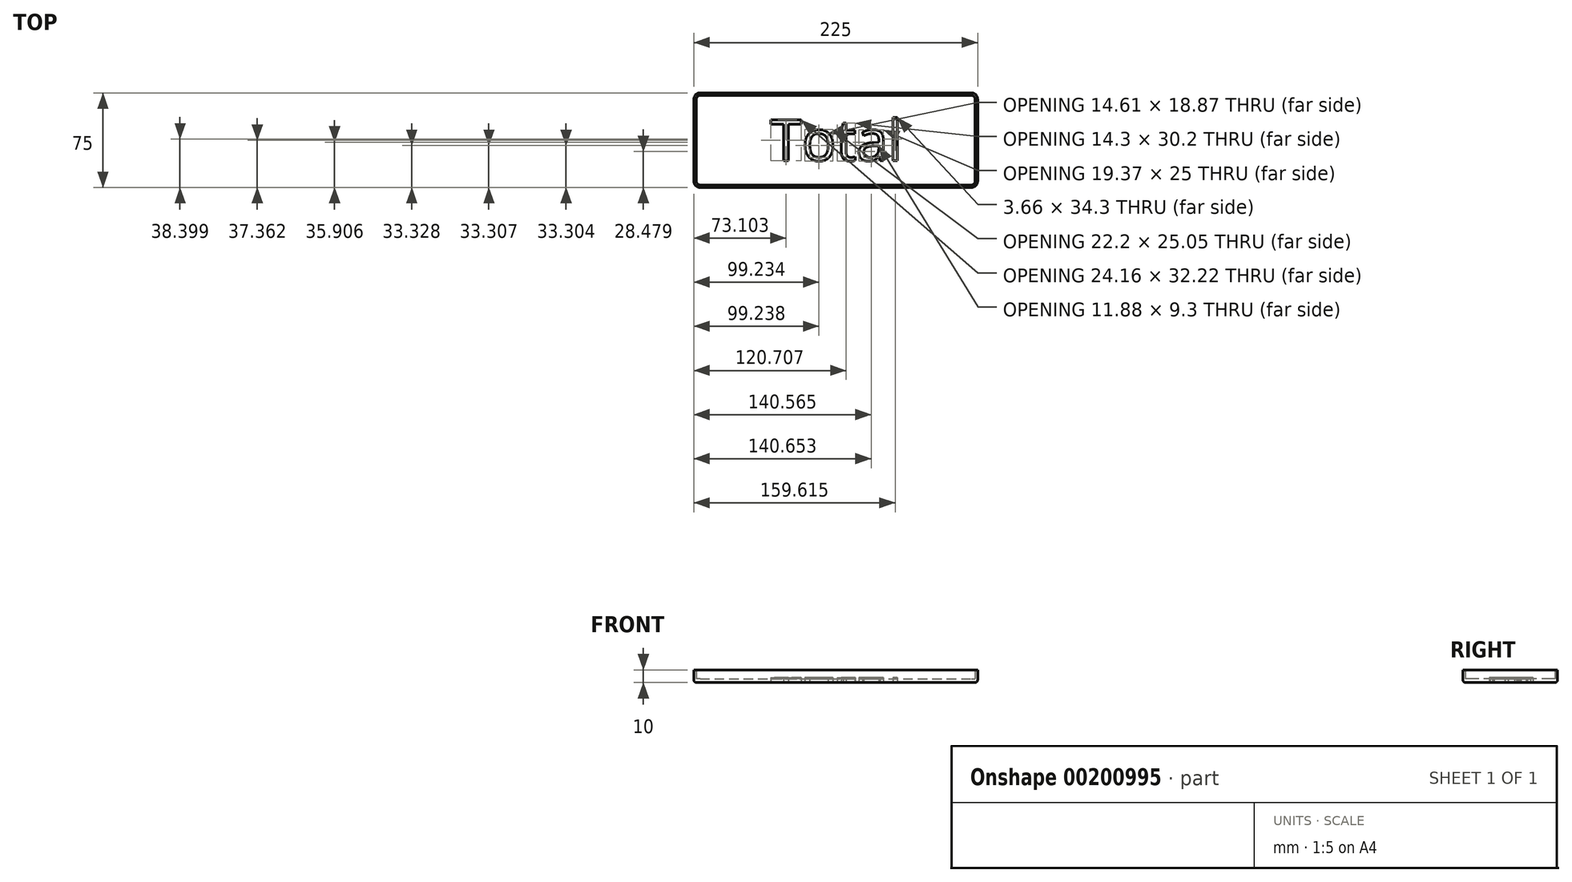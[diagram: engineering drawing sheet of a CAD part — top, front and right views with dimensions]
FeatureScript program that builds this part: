
annotation { "Feature Type Name" : "Feature", "Feature Type Description" : "" }
export const myFeature = defineFeature(function(context is Context, id is Id, definition is map)
    precondition{}
    {
        {
            var Q0;
            Q0=qCreatedBy(makeId("Top.planeOp"),FACE);
            var sketch = newSketch(context, id + "F0", { "sketchPlane" : qUnion([Q0])});
            skLineSegment(sketch, "E0.bottom", {"start": v(-41.61, 75) * mm, "end": v(173.39, 75) * mm});
            skLineSegment(sketch, "E0.top", {"start": v(-41.61, 0) * mm, "end": v(173.39, 0) * mm});
            skLineSegment(sketch, "E0.left", {"start": v(-46.61, 70) * mm, "end": v(-46.61, 5) * mm});
            skLineSegment(sketch, "E0.right", {"start": v(178.39, 70) * mm, "end": v(178.39, 5) * mm});
            skLineSegment(sketch, "E1.0", {"start": v(-41.61, 2) * mm, "end": v(173.39, 2) * mm});
            skLineSegment(sketch, "E1.1", {"start": v(-44.61, 70) * mm, "end": v(-44.61, 5) * mm});
            skLineSegment(sketch, "E1.2", {"start": v(-41.61, 73) * mm, "end": v(173.39, 73) * mm});
            skLineSegment(sketch, "E1.3", {"start": v(176.39, 70) * mm, "end": v(176.39, 5) * mm});
            skLineSegment(sketch, "E2", {"start": v(65.89, 73) * mm, "end": v(65.89, 2) * mm, "construction": true});
            skText(sketch, "E3", { "text": "Total", "fontName": "OpenSans-Regular.ttf"});
            skLineSegment(sketch, "E4", {"start": v(117.76, 37.5) * mm, "end": v(14.02, 37.5) * mm, "construction": true});
            skLineSegment(sketch, "E5", {"start": v(65.89, 37.5) * mm, "end": v(176.39, 37.5) * mm, "construction": true});
            skPoint(sketch, "E6.visualSharp", {"position": v(176.39, 73) * mm});
            skArc(sketch, "E6.filletArc", {"start": v(176.39, 70) * mm, "mid": v(175.5, 72.12) * mm, "end": v(173.39, 73) * mm});
            skPoint(sketch, "E7.visualSharp", {"position": v(-44.61, 73) * mm});
            skArc(sketch, "E7.filletArc", {"start": v(-41.61, 73) * mm, "mid": v(-43.73, 72.12) * mm, "end": v(-44.61, 70) * mm});
            skPoint(sketch, "E8.visualSharp", {"position": v(-44.61, 2) * mm});
            skArc(sketch, "E8.filletArc", {"start": v(-44.61, 5) * mm, "mid": v(-43.73, 2.88) * mm, "end": v(-41.61, 2) * mm});
            skPoint(sketch, "E9.visualSharp", {"position": v(176.39, 2) * mm});
            skArc(sketch, "E9.filletArc", {"start": v(173.39, 2) * mm, "mid": v(175.5, 2.88) * mm, "end": v(176.39, 5) * mm});
            skPoint(sketch, "E10.visualSharp", {"position": v(178.39, 0) * mm});
            skArc(sketch, "E10.filletArc", {"start": v(173.39, 0) * mm, "mid": v(176.92, 1.46) * mm, "end": v(178.39, 5) * mm});
            skPoint(sketch, "E11.visualSharp", {"position": v(178.39, 75) * mm});
            skArc(sketch, "E11.filletArc", {"start": v(178.39, 70) * mm, "mid": v(176.92, 73.54) * mm, "end": v(173.39, 75) * mm});
            skPoint(sketch, "E12.visualSharp", {"position": v(-46.61, 75) * mm});
            skArc(sketch, "E12.filletArc", {"start": v(-41.61, 75) * mm, "mid": v(-45.15, 73.54) * mm, "end": v(-46.61, 70) * mm});
            skPoint(sketch, "E13.visualSharp", {"position": v(-46.61, 0) * mm});
            skArc(sketch, "E13.filletArc", {"start": v(-46.61, 5) * mm, "mid": v(-45.15, 1.46) * mm, "end": v(-41.61, 0) * mm});
            const initialGuessF0  = {"E3": [0.01402, 0.02125, 1, 0, 0.0325]};
            skSetInitialGuess(sketch, initialGuessF0);
            skSolve(sketch);
        }
        {
            var Q0;
            Q0=makeQuery(id+"F0.imprint","IMPRINT",FACE,{"disambiguationData":[TD([[makeQuery(id+"F0.imprint","IMPRINT",EDGE,{"derivedFrom":sQuery(id+"F0.wireOp",EDGE,"E1.0")}),1.0]])]});
            var Q1;
            Q1=makeQuery(id+"F0.imprint","IMPRINT",FACE,{"disambiguationData":[TD([[makeQuery(id+"F0.imprint","IMPRINT",EDGE,{"derivedFrom":sQuery(id+"F0.wireOp",EDGE,"E3.sketch_text.stroke-63")}),1.0]])]});
            var Q2;
            Q2=makeQuery(id+"F0.imprint","IMPRINT",FACE,{"disambiguationData":[TD([[makeQuery(id+"F0.imprint","IMPRINT",EDGE,{"derivedFrom":sQuery(id+"F0.wireOp",EDGE,"E3.sketch_text.stroke-17")}),1.0]])]});
            extrude(context, id + "F1", {"entities" : qUnion([Q0, Q1, Q2]), "depth" : 3 * mm});
        }
        {
            var Q0;
            Q0=makeQuery(id+"F0.imprint","IMPRINT",FACE,{"disambiguationData":[TD([[makeQuery(id+"F0.imprint","IMPRINT",EDGE,{"derivedFrom":sQuery(id+"F0.wireOp",EDGE,"E0.bottom")}),-1.0]])]});
            extrude(context, id + "F2", {"entities" : qUnion([Q0]), "operationType" : NewBodyOperationType.ADD, "depth" : 10 * mm});
        }
        {
            var Q0;
            Q0=makeQuery(id+"F0.imprint","IMPRINT",FACE,{"disambiguationData":[TD([[makeQuery(id+"F0.imprint","IMPRINT",EDGE,{"derivedFrom":sQuery(id+"F0.wireOp",EDGE,"E3.sketch_text.stroke-0")}),-1.0]])]});
            var Q1;
            Q1=makeQuery(id+"F0.imprint","IMPRINT",FACE,{"disambiguationData":[TD([[makeQuery(id+"F0.imprint","IMPRINT",EDGE,{"derivedFrom":sQuery(id+"F0.wireOp",EDGE,"E3.sketch_text.stroke-8")}),-1.0]])]});
            var Q2;
            Q2=makeQuery(id+"F0.imprint","IMPRINT",FACE,{"disambiguationData":[TD([[makeQuery(id+"F0.imprint","IMPRINT",EDGE,{"derivedFrom":sQuery(id+"F0.wireOp",EDGE,"E3.sketch_text.stroke-25")}),-1.0]])]});
            var Q3;
            Q3=makeQuery(id+"F0.imprint","IMPRINT",FACE,{"disambiguationData":[TD([[makeQuery(id+"F0.imprint","IMPRINT",EDGE,{"derivedFrom":sQuery(id+"F0.wireOp",EDGE,"E3.sketch_text.stroke-44")}),-1.0]])]});
            var Q4;
            Q4=makeQuery(id+"F0.imprint","IMPRINT",FACE,{"disambiguationData":[TD([[makeQuery(id+"F0.imprint","IMPRINT",EDGE,{"derivedFrom":sQuery(id+"F0.wireOp",EDGE,"E3.sketch_text.stroke-71")}),-1.0]])]});
            extrude(context, id + "F3", {"entities" : qUnion([Q0, Q1, Q2, Q3, Q4]), "depth" : 4 * mm});
        }
        {
            var Q0;
            Q0=makeQuery(id+"F2.opExtrude","CAP_EDGE",EDGE,{"disambiguationData":[OSD([sQuery(id+"F0.wireOp",EDGE,"E0.bottom")])],"isStart":true});
            fillet(context, id + "F4", {"entities" : qUnion([Q0]), "radius" : 2 * mm, "tangentPropagation" : true, "allowEdgeOverflow" : false});
        }
    });
